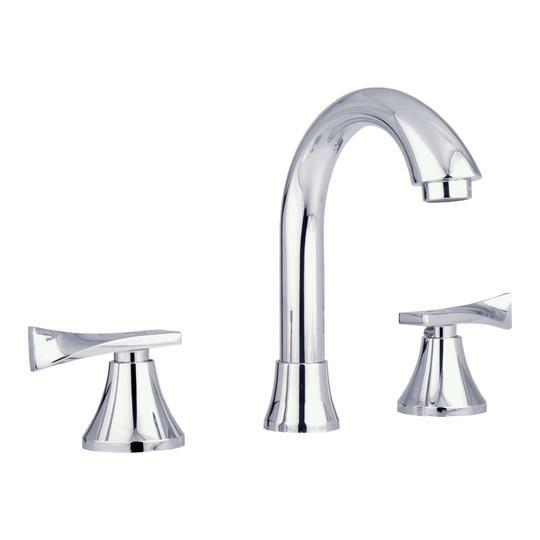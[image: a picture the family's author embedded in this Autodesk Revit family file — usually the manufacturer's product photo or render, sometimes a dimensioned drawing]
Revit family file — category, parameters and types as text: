
# Revit family: 01-2803-11 MEZCLADOR LAVAMANOS PLÁSTICO 8” PRISTINA
name_source: partatom
category: Plumbing Fixtures
revit_build: Autodesk Revit 2018 (Build: 20170223_1515(x64)
units: mm (PartAtom-declared; Revit-internal decimal feet)

## family parameters
Cut with Voids When Loaded = No
Host = Face
OmniClass Number = 23.31.11.00
Part Type = Normal
Room Calculation Point = No
Round Connector Dimension = Use Diameter
Shared = No

## types (1)
- 01-2803-11
    Alto - Aireador = 136 mm
    Alto manija = 54.8 mm
    Ancho manija = 75 mm
    CW Connection = Yes
    Default Elevation = 0 mm  [stored 0 ft]
    Description = Bimando baño
    Eje-Aireador = 136 mm
    Escudo = 60 mm
    HW Connection = Yes
    Link Ficha Tecnica = No encontrada en internet
    Manufacturer = Gricol
    Metal Zamak Cromado = Metal Zamak Cromado
    Model = 01-2803-11
    Plastico - ABS Cromado = Plastico - ABS Cromado
    Product Name = MEZCLADOR LAVAMANOS PLÁSTICO 8” PRISTINA
    Rosca - Rosca = 203.2 mm  [stored 0.666667 ft]
    Type Image = MEZCLADOR LAVAMANOS PLÁSTICO 8” PRISTINA.jpg
    URL = https://www.gricol.com
    Vent Connection = No
    Waste Connection = No

note: [stored X ft] marks values corroborated as IEEE doubles in the binary element streams (Revit-internal decimal feet)

## geometry (parser evidence)
native form markers: Blend x2, Sweep x6
no freeform markers — native parametric forms only
